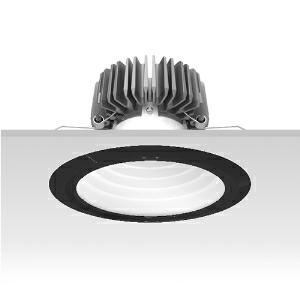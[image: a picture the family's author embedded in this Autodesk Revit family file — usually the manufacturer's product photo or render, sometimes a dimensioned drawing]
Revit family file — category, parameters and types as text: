
# Revit family: 3f_filippi_-_3f_reno_bianco_ampio_3f_filippi_-_30691_a01026_-_3f_reno_200_wh_4000-930_dali_wide___vt_bk_58cb
name_source: partatom
category: Lighting Fixtures
units: mm (PartAtom-declared; Revit-internal decimal feet)

## family parameters
Cut with Voids When Loaded = No
Host = Face
Light Source = No
Part Type = Normal
Room Calculation Point = No
Round Connector Dimension = Use Diameter
Shared = No

## types (1)
- 3F Filippi - 3F Reno Bianco Ampio (1 x LED, 3064 lm, 43 W, 3000 K)
    Apparent Load = 43 VA
    Approval mark = CE
    CIE Flux Codes = 75 94 99 100 100
    Color Rendering = 90
    Color Temperature = 3000 K
    Control Gear = Electronic transformer
    Default Elevation = 1800 mm
    Description = ILLUMINOTECHNICAL
Luminous efficiency 100% (DLOR 100%, ULOR 0%).
Initial luminous flux of the luminaire 3064 lm.
Direct symmetric wide distribution.
Installation Interdistance Transv.D = 1.56 x hu - Long.D = 1.56 x hu.
Tabular UGR (CIE 117 - 4H-8H; S=0.25H; 70/50/20): RUG 22.4 - 22.3.
Beam angle: 74° - 74°.
Luminous efficacy 71 lm/W.
Lifetime (L90/B10): 30000 h. (tq+25°C)
Lifetime (L85/B10): 50000 h. (tq+25°C)
Lifetime (L70/B10): 80000 h. (tq+25°C)
Sudden decreased luminous flux after 50000 hours: 0% (C0).
Photobiological safety in compliance with IEC/TR 62778: RG1 low risk, (IEC 62471).
In compliance with IEC/EN 62722-2-1 - IEC/EN 62717 standards.

SOURCE
Compact LED module 4000/930.
Energy efficiency class (UE 2019/2020 - UE 2019/2015): F.
CIE 13.3 Colour rendering index: CRI >90 (R9 >50%).
IES TM-30 Fidelity Index: Rf = 92 Rg = 101.
CCT nominal colour temperature 3000 K.
Colour initial tolerance (MacAdam): SDCM 3.
Zhaga Book 3 compliant.

MECHANICAL
Passive heat dissipator in die-casting aluminium, oversized, for optimum thermal management of the LED module.
Parabolic element with graduated/concentric rings in white polycarbonate.
Transparent external lens with glossy and satin differentiated surfaces, with a cooling and anti-insect system in methacrylate (PMMA).
Fastening spring clips in stainless steel.
Dimensions: diameter 226 mm, height 146 mm. Weight 1.785 kg.
IP44 protection degree for exposed part, IP20 for recessed part.
Mechanical strength to impacts IK06 (1 joule).
Glow-wire test resistance 650°C.

ELECTRICAL
Wiring on a separate unit.
Halogen Free DALI-2 DATI (Parts 251, 252, 253), PUSH-DIM, electronic wiring 230V-50/60Hz, power factor 0.97 at full load, THD <25%, constant output current, SELV, class II, 1 driver, 1 DALI addresse.
Power of the luminaire 43 W.
ENEC - CE.
SAFE FLICKER: PstLM=<1 and SVM=<0.4 (IEC TR 61547-1 and IEC TR 63158), to ensure a more comfortable and safe light.
Luminaire compliant with EN 60598-2-22 for power supply from a centralised emergency system CPSS (Central Power Supply System), not incorporated in the luminaire - high risk areas excluded. The default power and flux are 100% in AC and 100% in DC.
Ambient temperature from 0°C to +25°C.
Temperature class T6 max 85°C.
Relative humidity UR: <85%.

INSTALLATION
Pull-up recessed fitting.
False ceiling carving: 200 mm.
All accessories dedicated to this product are available on the Catalog and on our website www.3F-Filippi.com.

ACCESSORIES
A01026 - VT transparent glass, tempered, not flammable, locked and in line with the trim, in black polycarbonate.

APPLICATIONS
Environments: architectural, commercial, exhibition areas, transit areas, corridors, shops, display windows, service areas.
In false ceilings with narrow voids.

LIGHT MANAGEMENT
Recommended minimum setting: 10%.
The luminaire, equipped with (DALI-2 DATI) driver, can be controlled manually with 3F Easy Dim technology or automatically/manually with wired or wireless DALI/D2D control systems.
The D2D driver guarantees interoperability with other devices with the same certification by making the following information available:
Device Data (Part 251), Energy Report (Part 252), Diagnosis & Maintenance (Part 253).
In electrical systems without a regulation system (manual or automatic) and DALI bus, a suitable jumper must be made on the DA-DA terminals of the appliance.

WARNING
Luminaire designed for disposal/recycling at end-of-life.
Replaceable (LED only) light source by a professional. Replaceable control gear by a professional.
    Height = 0 mm  [stored 0 ft]
    Lamp = 1 x LED
    Lamp Light Flux = 3064 lm
    Lamp Power = 43 W
    Lamp count = 1
    Length = 226 mm
    Lifetime = 50000 h
    Luminous efficacy = 71 lm/W
    Manufacturer = 3F Filippi
    ModVariant = No
    Model = 3F Filippi - 30691+A01026 - 3F Reno 200 WH 4000-930 DALI WIDE + VT BK
    Mounting Place = Ceiling
    Mounting Type = Recessed
    Number of Poles = 1
    OnlyDefault = Yes
    Power Factor = 1
    Product Name = 3F Filippi - 3F Reno Bianco Ampio
    Product group = recessed luminaire
    ProductGroupID = 4
    Protection Class = Protection class II
    Protection Degree = IP 20
    RLX_Detail_Level = 1
    RLX_Emergency_Light_Flux = 0 lm
    RLX_Emergency_Type = 0
    RLX_Emergency_Type_DB = No
    RlxData = <blob elided: 103737 chars, md5=3b886104>
    Socket = socket
    Standby Power = 0 W
    System Light Flux = 3064 lm
    System Power = 43 W
    Type Comments = Product without accessories
    Type Image = 3ffilippi_3f_reno_200_wh__a01026.jpg
    URL = http://relux.com
    VarID = ---
    Voltage = 0 V
    Weight = 0.00 kg
    Width = 0 mm  [stored 0 ft]

note: [stored X ft] marks values corroborated as IEEE doubles in the binary element streams (Revit-internal decimal feet)

## geometry (parser evidence)
native form markers: Blend x4, Sweep x9
no freeform markers — native parametric forms only
